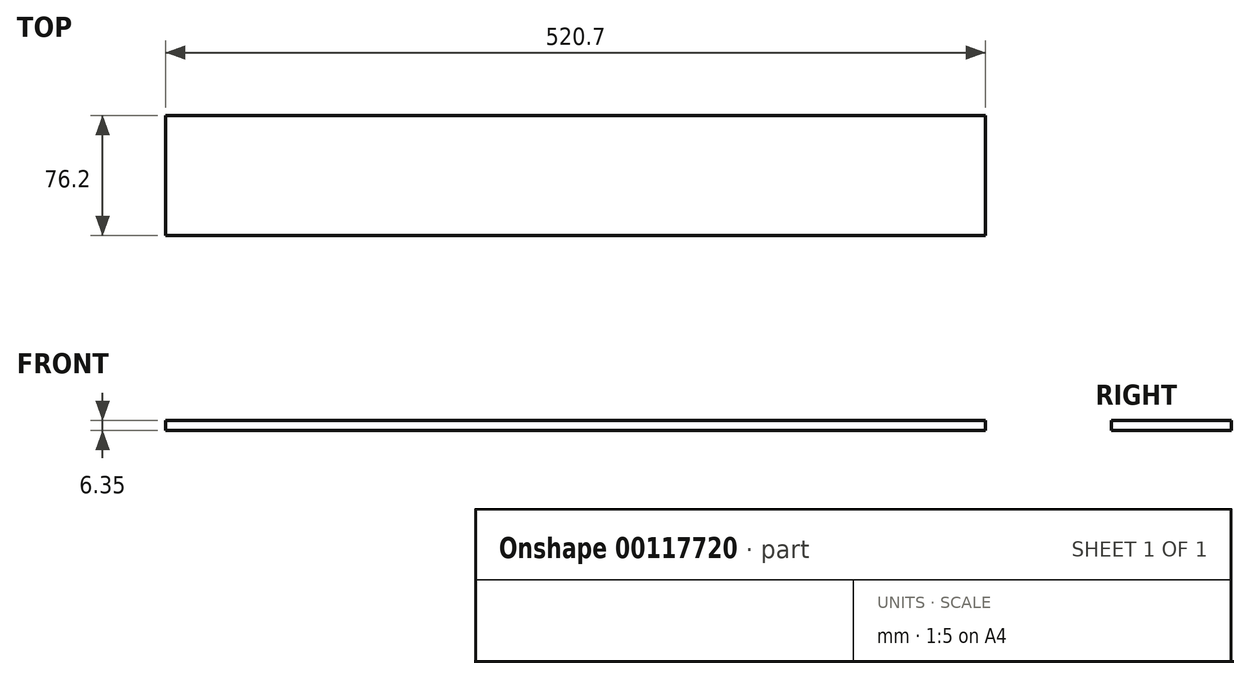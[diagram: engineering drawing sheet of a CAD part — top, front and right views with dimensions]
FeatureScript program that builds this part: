
annotation { "Feature Type Name" : "Feature", "Feature Type Description" : "" }
export const myFeature = defineFeature(function(context is Context, id is Id, definition is map)
    precondition{}
    {
        {
            var Q0;
            Q0=qCreatedBy(makeId("Top.planeOp"),FACE);
            var sketch = newSketch(context, id + "F0", { "sketchPlane" : qUnion([Q0])});
            skLineSegment(sketch, "E0.bottom", {"start": v(-265.91, 37.74) * mm, "end": v(254.79, 37.74) * mm});
            skLineSegment(sketch, "E0.top", {"start": v(-265.91, -38.46) * mm, "end": v(254.79, -38.46) * mm});
            skLineSegment(sketch, "E0.left", {"start": v(-265.91, 37.74) * mm, "end": v(-265.91, -38.46) * mm});
            skLineSegment(sketch, "E0.right", {"start": v(254.79, 37.74) * mm, "end": v(254.79, -38.46) * mm});
            skSolve(sketch);
        }
        {
            var Q0;
            Q0 = qSketchRegion(id + "F0", true);
            extrude(context, id + "F1", {"entities" : qUnion([Q0]), "depth" : 6.35 * mm});
        }
    });
